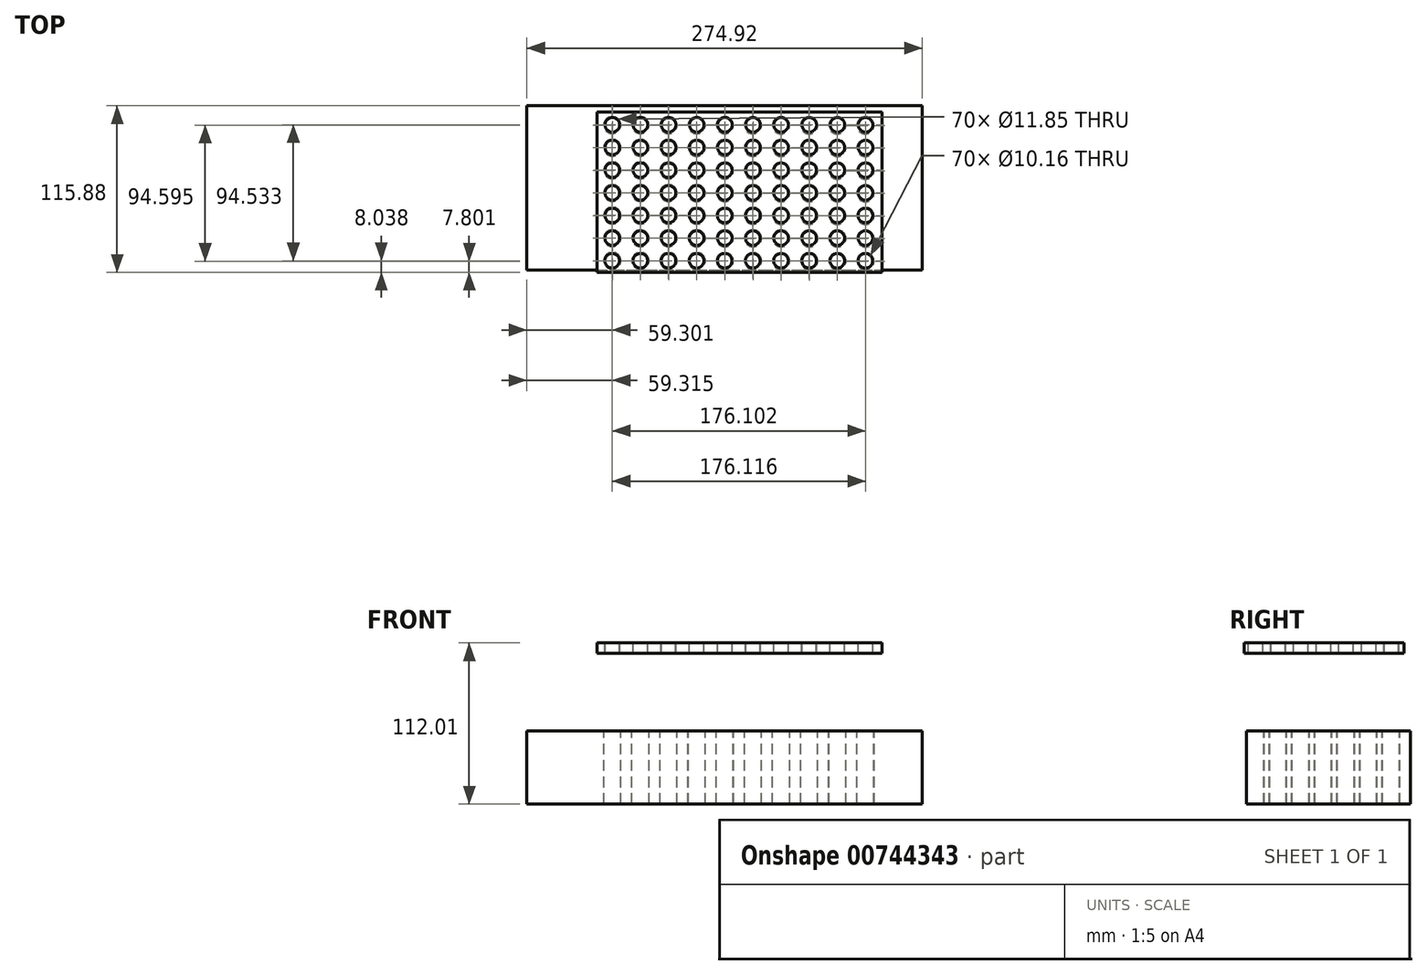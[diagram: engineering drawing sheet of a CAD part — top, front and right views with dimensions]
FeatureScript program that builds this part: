
annotation { "Feature Type Name" : "Feature", "Feature Type Description" : "" }
export const myFeature = defineFeature(function(context is Context, id is Id, definition is map)
    precondition{}
    {
        {
            var Q0;
            Q0=qCreatedBy(makeId("Top.planeOp"),FACE);
            var sketch = newSketch(context, id + "F0", { "sketchPlane" : qUnion([Q0])});
            skLineSegment(sketch, "E0.bottom", {"start": v(-98.84, 55.5) * mm, "end": v(99.49, 55.5) * mm});
            skLineSegment(sketch, "E0.top", {"start": v(-98.84, -55.83) * mm, "end": v(99.49, -55.83) * mm});
            skLineSegment(sketch, "E0.left", {"start": v(-98.84, 55.5) * mm, "end": v(-98.84, -55.83) * mm});
            skLineSegment(sketch, "E0.right", {"start": v(99.49, 55.5) * mm, "end": v(99.49, -55.83) * mm});
            skCircle(sketch, "E1", {"center": v(-88.12, 46.74) * mm, "radius": 5.08 * mm});
            skCircle(sketch, "E2.0.1.0", {"center": v(-88.14, 31) * mm, "radius": 5.08 * mm});
            skCircle(sketch, "E2.0.2.0", {"center": v(-88.16, 15.24) * mm, "radius": 5.08 * mm});
            skCircle(sketch, "E2.0.3.0", {"center": v(-88.17, -0.5) * mm, "radius": 5.08 * mm});
            skCircle(sketch, "E2.0.4.0", {"center": v(-88.19, -16.25) * mm, "radius": 5.08 * mm});
            skCircle(sketch, "E2.0.5.0", {"center": v(-88.2, -32) * mm, "radius": 5.08 * mm});
            skCircle(sketch, "E2.0.6.0", {"center": v(-88.22, -47.75) * mm, "radius": 5.08 * mm});
            skCircle(sketch, "E2.1.0.0", {"center": v(-68.57, 46.74) * mm, "radius": 5.08 * mm});
            skCircle(sketch, "E2.1.1.0", {"center": v(-68.58, 30.99) * mm, "radius": 5.08 * mm});
            skCircle(sketch, "E2.1.2.0", {"center": v(-68.6, 15.24) * mm, "radius": 5.08 * mm});
            skCircle(sketch, "E2.1.3.0", {"center": v(-68.61, -0.5) * mm, "radius": 5.08 * mm});
            skCircle(sketch, "E2.1.4.0", {"center": v(-68.63, -16.26) * mm, "radius": 5.08 * mm});
            skCircle(sketch, "E2.1.5.0", {"center": v(-68.64, -32) * mm, "radius": 5.08 * mm});
            skCircle(sketch, "E2.1.6.0", {"center": v(-68.66, -47.75) * mm, "radius": 5.08 * mm});
            skCircle(sketch, "E2.2.0.0", {"center": v(-49, 46.73) * mm, "radius": 5.08 * mm});
            skCircle(sketch, "E2.2.1.0", {"center": v(-49.02, 30.98) * mm, "radius": 5.08 * mm});
            skCircle(sketch, "E2.2.2.0", {"center": v(-49.04, 15.23) * mm, "radius": 5.08 * mm});
            skCircle(sketch, "E2.2.3.0", {"center": v(-49.06, -0.51) * mm, "radius": 5.08 * mm});
            skCircle(sketch, "E2.2.4.0", {"center": v(-49.07, -16.26) * mm, "radius": 5.08 * mm});
            skCircle(sketch, "E2.2.5.0", {"center": v(-49.09, -32) * mm, "radius": 5.08 * mm});
            skCircle(sketch, "E2.2.6.0", {"center": v(-49.1, -47.76) * mm, "radius": 5.08 * mm});
            skCircle(sketch, "E2.3.0.0", {"center": v(-29.45, 46.73) * mm, "radius": 5.08 * mm});
            skCircle(sketch, "E2.3.1.0", {"center": v(-29.47, 30.98) * mm, "radius": 5.08 * mm});
            skCircle(sketch, "E2.3.2.0", {"center": v(-29.48, 15.23) * mm, "radius": 5.08 * mm});
            skCircle(sketch, "E2.3.3.0", {"center": v(-29.5, -0.52) * mm, "radius": 5.08 * mm});
            skCircle(sketch, "E2.3.4.0", {"center": v(-29.51, -16.27) * mm, "radius": 5.08 * mm});
            skCircle(sketch, "E2.3.5.0", {"center": v(-29.53, -32.01) * mm, "radius": 5.08 * mm});
            skCircle(sketch, "E2.3.6.0", {"center": v(-29.54, -47.76) * mm, "radius": 5.08 * mm});
            skCircle(sketch, "E2.4.0.0", {"center": v(-9.9, 46.72) * mm, "radius": 5.08 * mm});
            skCircle(sketch, "E2.4.1.0", {"center": v(-9.9, 30.97) * mm, "radius": 5.08 * mm});
            skCircle(sketch, "E2.4.2.0", {"center": v(-9.92, 15.22) * mm, "radius": 5.08 * mm});
            skCircle(sketch, "E2.4.3.0", {"center": v(-9.94, -0.52) * mm, "radius": 5.08 * mm});
            skCircle(sketch, "E2.4.4.0", {"center": v(-9.96, -16.27) * mm, "radius": 5.08 * mm});
            skCircle(sketch, "E2.4.5.0", {"center": v(-9.97, -32.02) * mm, "radius": 5.08 * mm});
            skCircle(sketch, "E2.4.6.0", {"center": v(-9.99, -47.77) * mm, "radius": 5.08 * mm});
            skCircle(sketch, "E2.5.0.0", {"center": v(9.67, 46.72) * mm, "radius": 5.08 * mm});
            skCircle(sketch, "E2.5.1.0", {"center": v(9.65, 30.97) * mm, "radius": 5.08 * mm});
            skCircle(sketch, "E2.5.2.0", {"center": v(9.63, 15.22) * mm, "radius": 5.08 * mm});
            skCircle(sketch, "E2.5.3.0", {"center": v(9.62, -0.53) * mm, "radius": 5.08 * mm});
            skCircle(sketch, "E2.5.4.0", {"center": v(9.6, -16.28) * mm, "radius": 5.08 * mm});
            skCircle(sketch, "E2.5.5.0", {"center": v(9.59, -32.02) * mm, "radius": 5.08 * mm});
            skCircle(sketch, "E2.5.6.0", {"center": v(9.57, -47.77) * mm, "radius": 5.08 * mm});
            skCircle(sketch, "E2.6.0.0", {"center": v(29.22, 46.71) * mm, "radius": 5.08 * mm});
            skCircle(sketch, "E2.6.1.0", {"center": v(29.2, 30.96) * mm, "radius": 5.08 * mm});
            skCircle(sketch, "E2.6.2.0", {"center": v(29.2, 15.21) * mm, "radius": 5.08 * mm});
            skCircle(sketch, "E2.6.3.0", {"center": v(29.18, -0.53) * mm, "radius": 5.08 * mm});
            skCircle(sketch, "E2.6.4.0", {"center": v(29.16, -16.28) * mm, "radius": 5.08 * mm});
            skCircle(sketch, "E2.6.5.0", {"center": v(29.15, -32.03) * mm, "radius": 5.08 * mm});
            skCircle(sketch, "E2.6.6.0", {"center": v(29.13, -47.78) * mm, "radius": 5.08 * mm});
            skCircle(sketch, "E2.7.0.0", {"center": v(48.78, 46.7) * mm, "radius": 5.08 * mm});
            skCircle(sketch, "E2.7.1.0", {"center": v(48.77, 30.96) * mm, "radius": 5.08 * mm});
            skCircle(sketch, "E2.7.2.0", {"center": v(48.75, 15.2) * mm, "radius": 5.08 * mm});
            skCircle(sketch, "E2.7.3.0", {"center": v(48.73, -0.54) * mm, "radius": 5.08 * mm});
            skCircle(sketch, "E2.7.4.0", {"center": v(48.72, -16.29) * mm, "radius": 5.08 * mm});
            skCircle(sketch, "E2.7.5.0", {"center": v(48.7, -32.03) * mm, "radius": 5.08 * mm});
            skCircle(sketch, "E2.7.6.0", {"center": v(48.69, -47.78) * mm, "radius": 5.08 * mm});
            skCircle(sketch, "E2.8.0.0", {"center": v(68.34, 46.7) * mm, "radius": 5.08 * mm});
            skCircle(sketch, "E2.8.1.0", {"center": v(68.32, 30.95) * mm, "radius": 5.08 * mm});
            skCircle(sketch, "E2.8.2.0", {"center": v(68.3, 15.2) * mm, "radius": 5.08 * mm});
            skCircle(sketch, "E2.8.3.0", {"center": v(68.3, -0.54) * mm, "radius": 5.08 * mm});
            skCircle(sketch, "E2.8.4.0", {"center": v(68.28, -16.3) * mm, "radius": 5.08 * mm});
            skCircle(sketch, "E2.8.5.0", {"center": v(68.26, -32.04) * mm, "radius": 5.08 * mm});
            skCircle(sketch, "E2.8.6.0", {"center": v(68.25, -47.79) * mm, "radius": 5.08 * mm});
            skCircle(sketch, "E2.9.0.0", {"center": v(87.9, 46.7) * mm, "radius": 5.08 * mm});
            skCircle(sketch, "E2.9.1.0", {"center": v(87.88, 30.95) * mm, "radius": 5.08 * mm});
            skCircle(sketch, "E2.9.2.0", {"center": v(87.87, 15.2) * mm, "radius": 5.08 * mm});
            skCircle(sketch, "E2.9.3.0", {"center": v(87.85, -0.55) * mm, "radius": 5.08 * mm});
            skCircle(sketch, "E2.9.4.0", {"center": v(87.83, -16.3) * mm, "radius": 5.08 * mm});
            skCircle(sketch, "E2.9.5.0", {"center": v(87.82, -32.04) * mm, "radius": 5.08 * mm});
            skCircle(sketch, "E2.9.6.0", {"center": v(87.8, -47.8) * mm, "radius": 5.08 * mm});
            skLineSegment(sketch, "E2.direction1", {"start": v(-88.12, 46.74) * mm, "end": v(-68.57, 46.74) * mm, "construction": true});
            skLineSegment(sketch, "E2.direction2", {"start": v(-88.12, 46.74) * mm, "end": v(-88.14, 31) * mm, "construction": true});
            skSolve(sketch);
        }
        {
            var Q0;
            Q0=makeQuery(id+"F0.imprint","IMPRINT",FACE,{"disambiguationData":[TD([[makeQuery(id+"F0.imprint","IMPRINT",EDGE,{"derivedFrom":sQuery(id+"F0.wireOp",EDGE,"E0.bottom")}),-1.0]])]});
            extrude(context, id + "F1", {"entities" : qUnion([Q0]), "oppositeDirection" : true, "depth" : 7.11 * mm, "offsetDistance" : 25.4 * mm});
        }
        {
            var Q0;
            Q0=qCreatedBy(makeId("Top.planeOp"),FACE);
            cPlane(context, id + "F2", {"entities" : qUnion([Q0]), "cplaneType" : CPlaneType.OFFSET, "offset" : 61.2 * mm, "oppositeDirection" : true, "width" : 152.4 * mm, "height" : 152.4 * mm});
        }
        {
            var Q0;
            Q0=qCreatedBy(id+"F2.planeOp",FACE);
            var sketch = newSketch(context, id + "F3", { "sketchPlane" : qUnion([Q0])});
            skLineSegment(sketch, "E3.bottom", {"start": v(-147.52, -57.78) * mm, "end": v(127.4, -57.78) * mm});
            skLineSegment(sketch, "E3.top", {"start": v(-147.52, 60.05) * mm, "end": v(127.4, 60.05) * mm});
            skLineSegment(sketch, "E3.left", {"start": v(-147.52, -57.78) * mm, "end": v(-147.52, 60.05) * mm});
            skLineSegment(sketch, "E3.right", {"start": v(127.4, -57.78) * mm, "end": v(127.4, 60.05) * mm});
            skLineSegment(sketch, "E4", {"start": v(-147.52, -54.2) * mm, "end": v(127.4, -54.2) * mm});
            skCircle(sketch, "E5", {"center": v(-88.12, -47.72) * mm, "radius": 5.92 * mm});
            skCircle(sketch, "E6.0.1.0", {"center": v(-88.14, -32) * mm, "radius": 5.92 * mm});
            skCircle(sketch, "E6.0.2.0", {"center": v(-88.15, -16.3) * mm, "radius": 5.92 * mm});
            skCircle(sketch, "E6.0.3.0", {"center": v(-88.16, -0.58) * mm, "radius": 5.92 * mm});
            skCircle(sketch, "E6.0.4.0", {"center": v(-88.18, 15.14) * mm, "radius": 5.92 * mm});
            skCircle(sketch, "E6.0.5.0", {"center": v(-88.2, 30.85) * mm, "radius": 5.92 * mm});
            skCircle(sketch, "E6.0.6.0", {"center": v(-88.2, 46.57) * mm, "radius": 5.92 * mm});
            skCircle(sketch, "E6.1.0.0", {"center": v(-68.57, -47.75) * mm, "radius": 5.92 * mm});
            skCircle(sketch, "E6.1.1.0", {"center": v(-68.58, -32.04) * mm, "radius": 5.92 * mm});
            skCircle(sketch, "E6.1.2.0", {"center": v(-68.6, -16.32) * mm, "radius": 5.92 * mm});
            skCircle(sketch, "E6.1.3.0", {"center": v(-68.6, -0.61) * mm, "radius": 5.92 * mm});
            skCircle(sketch, "E6.1.4.0", {"center": v(-68.62, 15.1) * mm, "radius": 5.92 * mm});
            skCircle(sketch, "E6.1.5.0", {"center": v(-68.63, 30.82) * mm, "radius": 5.92 * mm});
            skCircle(sketch, "E6.1.6.0", {"center": v(-68.65, 46.53) * mm, "radius": 5.92 * mm});
            skCircle(sketch, "E6.2.0.0", {"center": v(-49, -47.79) * mm, "radius": 5.92 * mm});
            skCircle(sketch, "E6.2.1.0", {"center": v(-49.02, -32.07) * mm, "radius": 5.92 * mm});
            skCircle(sketch, "E6.2.2.0", {"center": v(-49.04, -16.36) * mm, "radius": 5.92 * mm});
            skCircle(sketch, "E6.2.3.0", {"center": v(-49.05, -0.65) * mm, "radius": 5.92 * mm});
            skCircle(sketch, "E6.2.4.0", {"center": v(-49.06, 15.07) * mm, "radius": 5.92 * mm});
            skCircle(sketch, "E6.2.5.0", {"center": v(-49.08, 30.78) * mm, "radius": 5.92 * mm});
            skCircle(sketch, "E6.2.6.0", {"center": v(-49.09, 46.5) * mm, "radius": 5.92 * mm});
            skCircle(sketch, "E6.3.0.0", {"center": v(-29.45, -47.82) * mm, "radius": 5.92 * mm});
            skCircle(sketch, "E6.3.1.0", {"center": v(-29.46, -32.1) * mm, "radius": 5.92 * mm});
            skCircle(sketch, "E6.3.2.0", {"center": v(-29.48, -16.4) * mm, "radius": 5.92 * mm});
            skCircle(sketch, "E6.3.3.0", {"center": v(-29.5, -0.68) * mm, "radius": 5.92 * mm});
            skCircle(sketch, "E6.3.4.0", {"center": v(-29.5, 15.03) * mm, "radius": 5.92 * mm});
            skCircle(sketch, "E6.3.5.0", {"center": v(-29.52, 30.75) * mm, "radius": 5.92 * mm});
            skCircle(sketch, "E6.3.6.0", {"center": v(-29.53, 46.46) * mm, "radius": 5.92 * mm});
            skCircle(sketch, "E6.4.0.0", {"center": v(-9.9, -47.86) * mm, "radius": 5.92 * mm});
            skCircle(sketch, "E6.4.1.0", {"center": v(-9.9, -32.14) * mm, "radius": 5.92 * mm});
            skCircle(sketch, "E6.4.2.0", {"center": v(-9.92, -16.43) * mm, "radius": 5.92 * mm});
            skCircle(sketch, "E6.4.3.0", {"center": v(-9.93, -0.71) * mm, "radius": 5.92 * mm});
            skCircle(sketch, "E6.4.4.0", {"center": v(-9.95, 15) * mm, "radius": 5.92 * mm});
            skCircle(sketch, "E6.4.5.0", {"center": v(-9.96, 30.71) * mm, "radius": 5.92 * mm});
            skCircle(sketch, "E6.4.6.0", {"center": v(-9.97, 46.43) * mm, "radius": 5.92 * mm});
            skCircle(sketch, "E6.5.0.0", {"center": v(9.67, -47.9) * mm, "radius": 5.92 * mm});
            skCircle(sketch, "E6.5.1.0", {"center": v(9.65, -32.18) * mm, "radius": 5.92 * mm});
            skCircle(sketch, "E6.5.2.0", {"center": v(9.64, -16.46) * mm, "radius": 5.92 * mm});
            skCircle(sketch, "E6.5.3.0", {"center": v(9.63, -0.75) * mm, "radius": 5.92 * mm});
            skCircle(sketch, "E6.5.4.0", {"center": v(9.61, 14.96) * mm, "radius": 5.92 * mm});
            skCircle(sketch, "E6.5.5.0", {"center": v(9.6, 30.68) * mm, "radius": 5.92 * mm});
            skCircle(sketch, "E6.5.6.0", {"center": v(9.58, 46.4) * mm, "radius": 5.92 * mm});
            skCircle(sketch, "E6.6.0.0", {"center": v(29.22, -47.93) * mm, "radius": 5.92 * mm});
            skCircle(sketch, "E6.6.1.0", {"center": v(29.2, -32.21) * mm, "radius": 5.92 * mm});
            skCircle(sketch, "E6.6.2.0", {"center": v(29.2, -16.5) * mm, "radius": 5.92 * mm});
            skCircle(sketch, "E6.6.3.0", {"center": v(29.18, -0.78) * mm, "radius": 5.92 * mm});
            skCircle(sketch, "E6.6.4.0", {"center": v(29.17, 14.93) * mm, "radius": 5.92 * mm});
            skCircle(sketch, "E6.6.5.0", {"center": v(29.16, 30.64) * mm, "radius": 5.92 * mm});
            skCircle(sketch, "E6.6.6.0", {"center": v(29.14, 46.36) * mm, "radius": 5.92 * mm});
            skCircle(sketch, "E6.7.0.0", {"center": v(48.78, -47.96) * mm, "radius": 5.92 * mm});
            skCircle(sketch, "E6.7.1.0", {"center": v(48.77, -32.25) * mm, "radius": 5.92 * mm});
            skCircle(sketch, "E6.7.2.0", {"center": v(48.75, -16.53) * mm, "radius": 5.92 * mm});
            skCircle(sketch, "E6.7.3.0", {"center": v(48.74, -0.82) * mm, "radius": 5.92 * mm});
            skCircle(sketch, "E6.7.4.0", {"center": v(48.73, 14.9) * mm, "radius": 5.92 * mm});
            skCircle(sketch, "E6.7.5.0", {"center": v(48.71, 30.6) * mm, "radius": 5.92 * mm});
            skCircle(sketch, "E6.7.6.0", {"center": v(48.7, 46.32) * mm, "radius": 5.92 * mm});
            skCircle(sketch, "E6.8.0.0", {"center": v(68.34, -48) * mm, "radius": 5.92 * mm});
            skCircle(sketch, "E6.8.1.0", {"center": v(68.33, -32.28) * mm, "radius": 5.92 * mm});
            skCircle(sketch, "E6.8.2.0", {"center": v(68.31, -16.57) * mm, "radius": 5.92 * mm});
            skCircle(sketch, "E6.8.3.0", {"center": v(68.3, -0.85) * mm, "radius": 5.92 * mm});
            skCircle(sketch, "E6.8.4.0", {"center": v(68.29, 14.86) * mm, "radius": 5.92 * mm});
            skCircle(sketch, "E6.8.5.0", {"center": v(68.27, 30.57) * mm, "radius": 5.92 * mm});
            skCircle(sketch, "E6.8.6.0", {"center": v(68.26, 46.29) * mm, "radius": 5.92 * mm});
            skCircle(sketch, "E6.9.0.0", {"center": v(87.9, -48.03) * mm, "radius": 5.92 * mm});
            skCircle(sketch, "E6.9.1.0", {"center": v(87.88, -32.32) * mm, "radius": 5.92 * mm});
            skCircle(sketch, "E6.9.2.0", {"center": v(87.87, -16.6) * mm, "radius": 5.92 * mm});
            skCircle(sketch, "E6.9.3.0", {"center": v(87.86, -0.89) * mm, "radius": 5.92 * mm});
            skCircle(sketch, "E6.9.4.0", {"center": v(87.84, 14.83) * mm, "radius": 5.92 * mm});
            skCircle(sketch, "E6.9.5.0", {"center": v(87.83, 30.54) * mm, "radius": 5.92 * mm});
            skCircle(sketch, "E6.9.6.0", {"center": v(87.82, 46.25) * mm, "radius": 5.92 * mm});
            skLineSegment(sketch, "E6.direction1", {"start": v(-88.12, -47.72) * mm, "end": v(-68.57, -47.75) * mm, "construction": true});
            skLineSegment(sketch, "E6.direction2", {"start": v(-88.12, -47.72) * mm, "end": v(-88.14, -32) * mm, "construction": true});
            skSolve(sketch);
        }
        {
            var Q0;
            {var subQ0=sQuery(id+"F3.wireOp",EDGE,"E3.top");Q0=makeQuery(id+"F3.imprint","IMPRINT",FACE,{"disambiguationData":[TD([[makeQuery(id+"F3.imprint","IMPRINT",EDGE,{"derivedFrom":subQ0}),-1.0]])]});}
            extrude(context, id + "F4", {"entities" : qUnion([Q0]), "oppositeDirection" : true, "depth" : 50.8 * mm, "offsetDistance" : 25.4 * mm});
        }
    });
